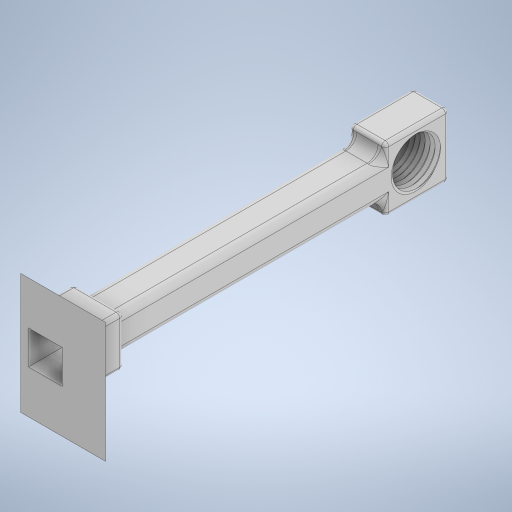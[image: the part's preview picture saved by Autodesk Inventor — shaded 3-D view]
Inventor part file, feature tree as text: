
AUTODESK INVENTOR PART (.ipt)
format: ipt  version: 2024 (Build 280153000, 153)  size: 716,288 bytes
history: native  units: mm
features: sketch x16, extrude x15, fillet x4, mirror x2, other x1
ambient origin geometry x8: Origin, YZ Plane, XZ Plane, XY Plane, X Axis, Y Axis, Z Axis, Center Point
bodies: Volumenkörper1 (feature_tree)
feature tree (38):
  extrude  "Extrusion1"  Depth=10.0mm
  extrude  "Extrusion2"  Depth=10.0mm
  extrude  "Extrusion3"  Depth=18.0mm TaperAngle=0.0deg
  extrude  "Extrusion4"  Depth=9.0mm TaperAngle=0.0deg
  other  "Spirale1"
  extrude  "Extrusion6"  Depth=9.0mm TaperAngle=0.0deg
  extrude  "Extrusion12"  Depth=1.7mm
  mirror  "Spiegeln1"
  extrude  "Extrusion13"  Depth=0.2mm
  mirror  "Spiegeln2"
  extrude  "Extrusion7"  Depth=9.5mm
  extrude  "Extrusion8"  Depth=9.75mm TaperAngle=0.0deg
  extrude  "Extrusion9"  Depth=1.5mm
  extrude  "Extrusion14"  Depth=1.5mm
  extrude  "Extrusion15"  Depth=1.5mm
  extrude  "Extrusion16"  Depth=2.0mm TaperAngle=0.0deg
  extrude  "Extrusion17"  Depth=15.0mm
  extrude  "Extrusion18"  Depth=2.0mm TaperAngle=0.0deg
  fillet  "Rundung3"  Radius=10.0mm
  fillet  "Rundung4"  Radius=10.0mm
  fillet  "Rundung5"  Radius=7.0mm
  fillet  "Rundung6"  Radius=10.0mm
  sketch  "Skizze1"  dims[d0=10.0mm d1=10.0mm]
  sketch  "Skizze2"  dims[d2=91.0mm d3=0.0mm d4=10.0mm]
  sketch  "Skizze3"  dims[d5=18.0mm d6=18.0mm d7=0.0mm]
  sketch  "Skizze4"  dims[d8=15.0mm d9=9.0mm d10=0.0mm]
  sketch  "Skizze5"  dims[d17=12.2mm d18=9.0mm d19=0.0mm]
  sketch  "Skizze7"  dims[d22=1.4mm d23=11.0mm d24=10.0mm d25=0.0mm d26=90.0deg d27=90.0deg d28=0.0mm d29=0.0mm d33=1.7mm]
  sketch  "Skizze8"  dims[d34=60.0deg d35=0.2mm]
  sketch  "Skizze9"  dims[d36=1.0mm d37=0.0mm d39=9.5mm]
  sketch  "Skizze10"  dims[d40=9.5mm d41=9.75mm d42=0.0mm]
  sketch  "Skizze16"  dims[d43=1.5mm d44=1.5mm]
  sketch  "Skizze17"  dims[d47=1.5mm d48=1.5mm]
  sketch  "Skizze18"  dims[d49=1.5mm d50=1.5mm]
  sketch  "Skizze20"  dims[d53=1.0mm d54=0.0mm d55=2.0mm d56=0.0mm]
  sketch  "Skizze22"  dims[d65=10.0mm d66=15.0mm]
  sketch  "Skizze23"  dims[d67=2.0mm d68=0.0mm d69=2.0mm d70=0.0mm d71=10.0mm d72=0.0mm d73=10.0mm d74=7.0mm d75=10.0mm]
  sketch  "Skizze24"  dims[d76=24.0mm d77=0.0mm d78=10.0mm d79=24.0mm d80=0.0mm d81=24.0mm d82=0.0mm d83=60.0mm d84=0.0mm d85=10.0mm d86=0.0mm d87=2.0mm d88=1.0mm d89=1.0mm d90=3.1mm d91=0.24mm d92=0.24mm d93=0.24mm d94=0.24mm d38=0.0mm]
